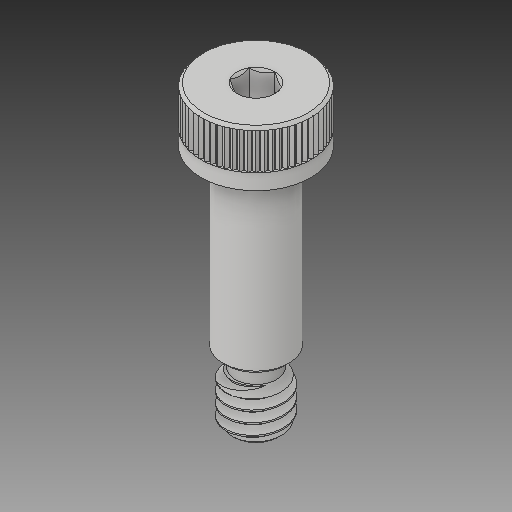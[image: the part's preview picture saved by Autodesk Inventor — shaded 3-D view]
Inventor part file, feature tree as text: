
AUTODESK INVENTOR PART (.ipt)
format: ipt  version: 2018 (Build 220112000, 112)  size: 681,984 bytes
history: native  units: in
note: dims shown in document units (in); Inventor stores cm internally (conversion verified against a paired STEP export)
features: chamfer x1
ambient origin geometry x8: Origin, YZ Plane, XZ Plane, XY Plane, X Axis, Y Axis, Z Axis, Center Point
bodies: Solid1 (feature_tree)
feature tree (1):
  chamfer  "Chamfer3"  [1 undecoded]
note: 1 required parameter value undecoded (feature->parameter linkage not recoverable at this tier; creation-order binding heuristic only, values carry confidence <= 0.55)
